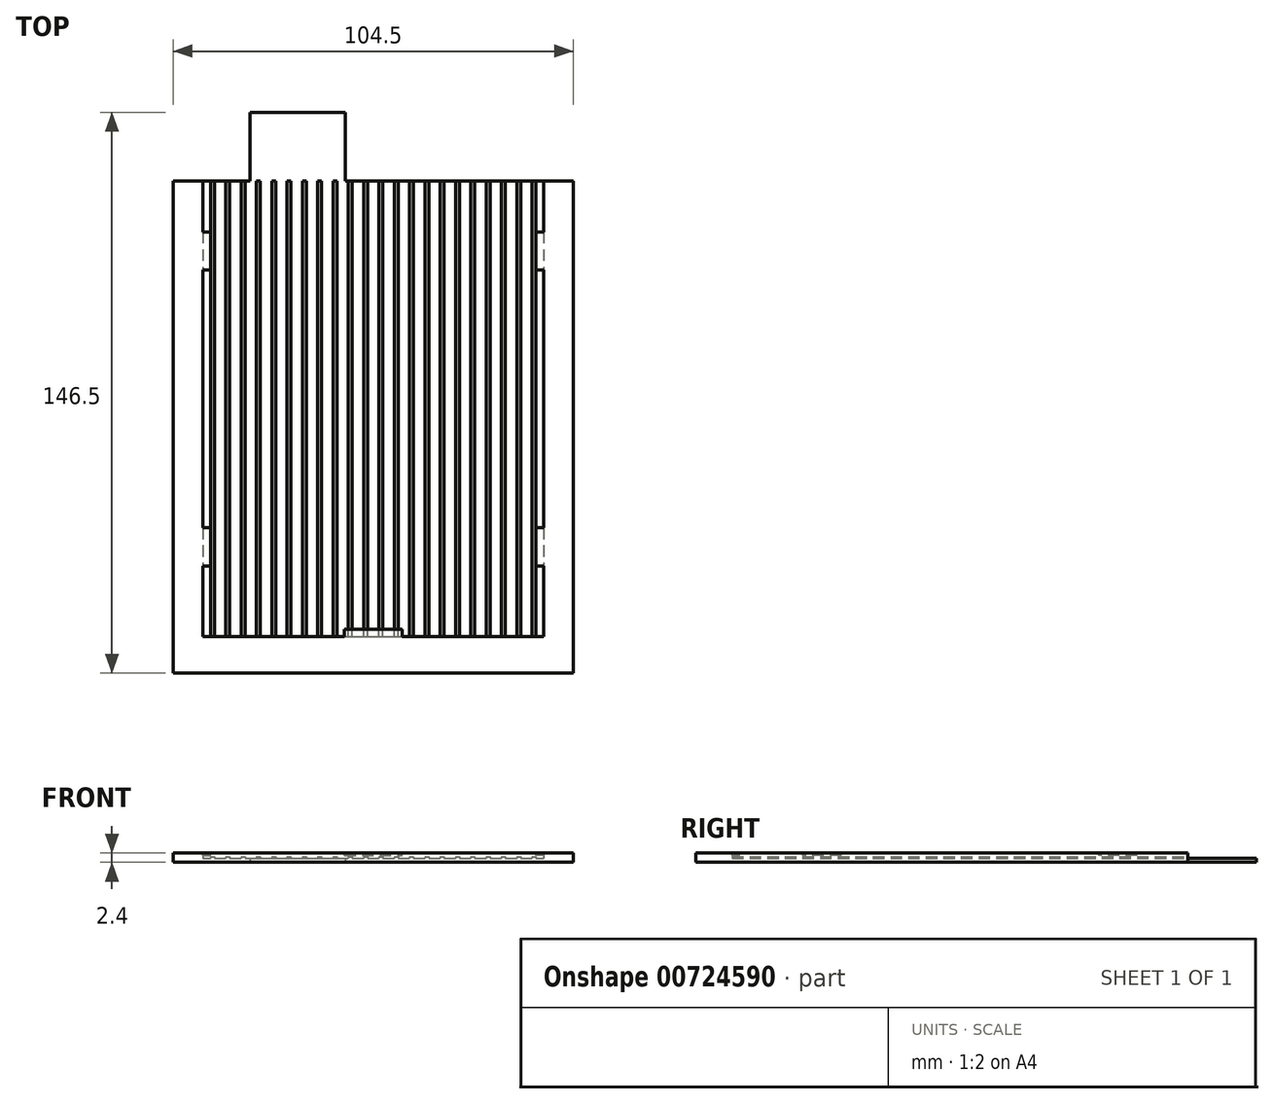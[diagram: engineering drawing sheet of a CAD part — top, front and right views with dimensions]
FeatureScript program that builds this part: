
annotation { "Feature Type Name" : "Feature", "Feature Type Description" : "" }
export const myFeature = defineFeature(function(context is Context, id is Id, definition is map)
    precondition{}
    {
        {
            var Q0;
            Q0=qCreatedBy(makeId("Top.planeOp"),FACE);
            var sketch = newSketch(context, id + "F0", { "sketchPlane" : qUnion([Q0])});
            skLineSegment(sketch, "E0.bottom", {"start": v(-45, 88.97) * mm, "end": v(-25, 88.97) * mm});
            skLineSegment(sketch, "E0.top", {"start": v(-45, -39.53) * mm, "end": v(59.5, -39.53) * mm});
            skLineSegment(sketch, "E0.left", {"start": v(-45, 88.97) * mm, "end": v(-45, -39.53) * mm});
            skLineSegment(sketch, "E0.right", {"start": v(59.5, 88.97) * mm, "end": v(59.5, -39.53) * mm});
            skLineSegment(sketch, "E1.top", {"start": v(-25, 106.97) * mm, "end": v(0, 106.97) * mm});
            skLineSegment(sketch, "E1.left", {"start": v(-25, 88.97) * mm, "end": v(-25, 106.97) * mm});
            skLineSegment(sketch, "E1.right", {"start": v(0, 88.97) * mm, "end": v(0, 106.97) * mm});
            skLineSegment(sketch, "E2.trimOffspring", {"start": v(0, 88.97) * mm, "end": v(59.5, 88.97) * mm});
            skSolve(sketch);
        }
        {
            var Q0;
            Q0=makeQuery(id+"F0.imprint","IMPRINT",FACE,{"disambiguationData":[TD([[makeQuery(id+"F0.imprint","IMPRINT",EDGE,{"derivedFrom":sQuery(id+"F0.wireOp",EDGE,"E0.bottom")}),-1.0]])]});
            extrude(context, id + "F1", {"entities" : qUnion([Q0]), "depth" : 1 * mm, "offsetDistance" : 25 * mm});
        }
        {
            var Q0;
            Q0=makeQuery(id+"F1.opExtrude","CAP_FACE",FACE,{"disambiguationData":[OSD([sQuery(id+"F0.wireOp",EDGE,"E0.bottom"),sQuery(id+"F0.wireOp",EDGE,"E0.top"),sQuery(id+"F0.wireOp",EDGE,"E0.left"),sQuery(id+"F0.wireOp",EDGE,"E0.right")])],"isStart":false});
            var sketch = newSketch(context, id + "F2", { "sketchPlane" : qUnion([Q0])});
            skLineSegment(sketch, "E3.bottom", {"start": v(-37.25, 88.97) * mm, "end": v(51.75, 88.97) * mm});
            skLineSegment(sketch, "E3.top", {"start": v(-37.25, -30.03) * mm, "end": v(51.75, -30.03) * mm});
            skLineSegment(sketch, "E3.left", {"start": v(-37.25, 88.97) * mm, "end": v(-37.25, -30.03) * mm});
            skLineSegment(sketch, "E3.right", {"start": v(51.75, 88.97) * mm, "end": v(51.75, -30.03) * mm});
            skSolve(sketch);
        }
        {
            var Q0;
            Q0=makeQuery(id+"F2.imprint","IMPRINT",FACE,{"disambiguationData":[TD([[makeQuery(id+"F2.imprint","IMPRINT",EDGE,{"derivedFrom":sQuery(id+"F2.wireOp",EDGE,"E3.top")}),-1.0]])]});
            extrude(context, id + "F3", {"entities" : qUnion([Q0]), "operationType" : NewBodyOperationType.ADD, "depth" : 1.4 * mm, "offsetDistance" : 25 * mm});
        }
        {
            var Q0;
            Q0=makeQuery(id+"F3.opExtrude","CAP_FACE",FACE,{"disambiguationData":[OSD([sQuery(id+"F0.wireOp",EDGE,"E0.bottom"),sQuery(id+"F0.wireOp",EDGE,"E0.top"),sQuery(id+"F0.wireOp",EDGE,"E0.left"),sQuery(id+"F0.wireOp",EDGE,"E0.right"),sQuery(id+"F0.wireOp",EDGE,"E2.trimOffspring"),sQuery(id+"F2.wireOp",EDGE,"E3.top"),sQuery(id+"F2.wireOp",EDGE,"E3.left"),sQuery(id+"F2.wireOp",EDGE,"E3.right")])],"isStart":false});
            var sketch = newSketch(context, id + "F4", { "sketchPlane" : qUnion([Q0])});
            skLineSegment(sketch, "E4.bottom", {"start": v(-37.25, 75.74) * mm, "end": v(-35.25, 75.74) * mm});
            skLineSegment(sketch, "E4.top", {"start": v(-37.25, 65.74) * mm, "end": v(-35.25, 65.74) * mm});
            skLineSegment(sketch, "E4.left", {"start": v(-37.25, 75.74) * mm, "end": v(-37.25, 65.74) * mm});
            skLineSegment(sketch, "E4.right", {"start": v(-35.25, 75.74) * mm, "end": v(-35.25, 65.74) * mm});
            skLineSegment(sketch, "E5.bottom", {"start": v(51.75, 75.74) * mm, "end": v(49.75, 75.74) * mm});
            skLineSegment(sketch, "E5.top", {"start": v(51.75, 65.74) * mm, "end": v(49.75, 65.74) * mm});
            skLineSegment(sketch, "E5.left", {"start": v(51.75, 75.74) * mm, "end": v(51.75, 65.74) * mm});
            skLineSegment(sketch, "E5.right", {"start": v(49.75, 75.74) * mm, "end": v(49.75, 65.74) * mm});
            skLineSegment(sketch, "E6.bottom", {"start": v(-37.25, -1.52) * mm, "end": v(-35.25, -1.52) * mm});
            skLineSegment(sketch, "E6.top", {"start": v(-37.25, -11.52) * mm, "end": v(-35.25, -11.52) * mm});
            skLineSegment(sketch, "E6.left", {"start": v(-37.25, -1.52) * mm, "end": v(-37.25, -11.52) * mm});
            skLineSegment(sketch, "E6.right", {"start": v(-35.25, -1.52) * mm, "end": v(-35.25, -11.52) * mm});
            skLineSegment(sketch, "E7.bottom", {"start": v(49.75, -1.52) * mm, "end": v(51.75, -1.52) * mm});
            skLineSegment(sketch, "E7.top", {"start": v(49.75, -11.52) * mm, "end": v(51.75, -11.52) * mm});
            skLineSegment(sketch, "E7.left", {"start": v(49.75, -1.52) * mm, "end": v(49.75, -11.52) * mm});
            skLineSegment(sketch, "E7.right", {"start": v(51.75, -1.52) * mm, "end": v(51.75, -11.52) * mm});
            skLineSegment(sketch, "E8.bottom", {"start": v(-0.25, -30.03) * mm, "end": v(14.75, -30.03) * mm});
            skLineSegment(sketch, "E8.top", {"start": v(-0.25, -28.03) * mm, "end": v(14.75, -28.03) * mm});
            skLineSegment(sketch, "E8.left", {"start": v(-0.25, -30.03) * mm, "end": v(-0.25, -28.03) * mm});
            skLineSegment(sketch, "E8.right", {"start": v(14.75, -30.03) * mm, "end": v(14.75, -28.03) * mm});
            skSolve(sketch);
        }
        {
            var Q0;
            Q0=makeQuery(id+"F4.imprint","IMPRINT",FACE,{"disambiguationData":[TD([[makeQuery(id+"F4.imprint","IMPRINT",EDGE,{"derivedFrom":sQuery(id+"F4.wireOp",EDGE,"E5.bottom")}),1.0]])]});
            var Q1;
            Q1=makeQuery(id+"F4.imprint","IMPRINT",FACE,{"disambiguationData":[TD([[makeQuery(id+"F4.imprint","IMPRINT",EDGE,{"derivedFrom":sQuery(id+"F4.wireOp",EDGE,"E7.bottom")}),-1.0]])]});
            var Q2;
            Q2=makeQuery(id+"F4.imprint","IMPRINT",FACE,{"disambiguationData":[TD([[makeQuery(id+"F4.imprint","IMPRINT",EDGE,{"derivedFrom":sQuery(id+"F4.wireOp",EDGE,"E8.bottom")}),1.0]])]});
            var Q3;
            Q3=makeQuery(id+"F4.imprint","IMPRINT",FACE,{"disambiguationData":[TD([[makeQuery(id+"F4.imprint","IMPRINT",EDGE,{"derivedFrom":sQuery(id+"F4.wireOp",EDGE,"E6.bottom")}),-1.0]])]});
            var Q4;
            Q4=makeQuery(id+"F4.imprint","IMPRINT",FACE,{"disambiguationData":[TD([[makeQuery(id+"F4.imprint","IMPRINT",EDGE,{"derivedFrom":sQuery(id+"F4.wireOp",EDGE,"E4.bottom")}),-1.0]])]});
            extrude(context, id + "F5", {"entities" : qUnion([Q0, Q1, Q2, Q3, Q4]), "operationType" : NewBodyOperationType.ADD, "depth" : -.6 * mm, "offsetDistance" : 25 * mm});
        }
        {
            var Q0;
            Q0=makeQuery(id+"F1.opExtrude","CAP_FACE",FACE,{"disambiguationData":[OSD([sQuery(id+"F0.wireOp",EDGE,"E0.bottom"),sQuery(id+"F0.wireOp",EDGE,"E0.top"),sQuery(id+"F0.wireOp",EDGE,"E0.left"),sQuery(id+"F0.wireOp",EDGE,"E0.right"),sQuery(id+"F0.wireOp",EDGE,"E1.top"),sQuery(id+"F0.wireOp",EDGE,"E1.left"),sQuery(id+"F0.wireOp",EDGE,"E1.right"),sQuery(id+"F0.wireOp",EDGE,"E2.trimOffspring")])],"isStart":false});
            var sketch = newSketch(context, id + "F6", { "sketchPlane" : qUnion([Q0])});
            skLineSegment(sketch, "E9.bottom", {"start": v(-35.25, -30.03) * mm, "end": v(-34.25, -30.03) * mm});
            skLineSegment(sketch, "E9.top", {"start": v(-35.25, 88.97) * mm, "end": v(-34.25, 88.97) * mm});
            skLineSegment(sketch, "E9.left", {"start": v(-35.25, -30.03) * mm, "end": v(-35.25, 88.97) * mm});
            skLineSegment(sketch, "E9.right", {"start": v(-34.25, -30.03) * mm, "end": v(-34.25, 88.97) * mm});
            skLineSegment(sketch, "E10.1.0.0", {"start": v(-30.25, -30.03) * mm, "end": v(-30.25, 88.97) * mm});
            skLineSegment(sketch, "E10.1.0.1", {"start": v(-31.25, -30.03) * mm, "end": v(-31.25, 88.97) * mm});
            skLineSegment(sketch, "E10.1.0.2", {"start": v(-31.25, 88.97) * mm, "end": v(-30.25, 88.97) * mm});
            skLineSegment(sketch, "E10.1.0.3", {"start": v(-31.25, -30.03) * mm, "end": v(-30.25, -30.03) * mm});
            skLineSegment(sketch, "E10.2.0.0", {"start": v(-26.25, -30.03) * mm, "end": v(-26.25, 88.97) * mm});
            skLineSegment(sketch, "E10.2.0.1", {"start": v(-27.25, -30.03) * mm, "end": v(-27.25, 88.97) * mm});
            skLineSegment(sketch, "E10.2.0.2", {"start": v(-27.25, 88.97) * mm, "end": v(-26.25, 88.97) * mm});
            skLineSegment(sketch, "E10.2.0.3", {"start": v(-27.25, -30.03) * mm, "end": v(-26.25, -30.03) * mm});
            skLineSegment(sketch, "E10.3.0.0", {"start": v(-22.25, -30.03) * mm, "end": v(-22.25, 88.97) * mm});
            skLineSegment(sketch, "E10.3.0.1", {"start": v(-23.25, -30.03) * mm, "end": v(-23.25, 88.97) * mm});
            skLineSegment(sketch, "E10.3.0.2", {"start": v(-23.25, 88.97) * mm, "end": v(-22.25, 88.97) * mm});
            skLineSegment(sketch, "E10.3.0.3", {"start": v(-23.25, -30.03) * mm, "end": v(-22.25, -30.03) * mm});
            skLineSegment(sketch, "E10.4.0.0", {"start": v(-18.25, -30.03) * mm, "end": v(-18.25, 88.97) * mm});
            skLineSegment(sketch, "E10.4.0.1", {"start": v(-19.25, -30.03) * mm, "end": v(-19.25, 88.97) * mm});
            skLineSegment(sketch, "E10.4.0.2", {"start": v(-19.25, 88.97) * mm, "end": v(-18.25, 88.97) * mm});
            skLineSegment(sketch, "E10.4.0.3", {"start": v(-19.25, -30.03) * mm, "end": v(-18.25, -30.03) * mm});
            skLineSegment(sketch, "E10.5.0.0", {"start": v(-14.25, -30.03) * mm, "end": v(-14.25, 88.97) * mm});
            skLineSegment(sketch, "E10.5.0.1", {"start": v(-15.25, -30.03) * mm, "end": v(-15.25, 88.97) * mm});
            skLineSegment(sketch, "E10.5.0.2", {"start": v(-15.25, 88.97) * mm, "end": v(-14.25, 88.97) * mm});
            skLineSegment(sketch, "E10.5.0.3", {"start": v(-15.25, -30.03) * mm, "end": v(-14.25, -30.03) * mm});
            skLineSegment(sketch, "E10.6.0.0", {"start": v(-10.25, -30.03) * mm, "end": v(-10.25, 88.97) * mm});
            skLineSegment(sketch, "E10.6.0.1", {"start": v(-11.25, -30.03) * mm, "end": v(-11.25, 88.97) * mm});
            skLineSegment(sketch, "E10.6.0.2", {"start": v(-11.25, 88.97) * mm, "end": v(-10.25, 88.97) * mm});
            skLineSegment(sketch, "E10.6.0.3", {"start": v(-11.25, -30.03) * mm, "end": v(-10.25, -30.03) * mm});
            skLineSegment(sketch, "E10.7.0.0", {"start": v(-6.25, -30.03) * mm, "end": v(-6.25, 88.97) * mm});
            skLineSegment(sketch, "E10.7.0.1", {"start": v(-7.25, -30.03) * mm, "end": v(-7.25, 88.97) * mm});
            skLineSegment(sketch, "E10.7.0.2", {"start": v(-7.25, 88.97) * mm, "end": v(-6.25, 88.97) * mm});
            skLineSegment(sketch, "E10.7.0.3", {"start": v(-7.25, -30.03) * mm, "end": v(-6.25, -30.03) * mm});
            skLineSegment(sketch, "E10.8.0.0", {"start": v(-2.25, -30.03) * mm, "end": v(-2.25, 88.97) * mm});
            skLineSegment(sketch, "E10.8.0.1", {"start": v(-3.25, -30.03) * mm, "end": v(-3.25, 88.97) * mm});
            skLineSegment(sketch, "E10.8.0.2", {"start": v(-3.25, 88.97) * mm, "end": v(-2.25, 88.97) * mm});
            skLineSegment(sketch, "E10.8.0.3", {"start": v(-3.25, -30.03) * mm, "end": v(-2.25, -30.03) * mm});
            skLineSegment(sketch, "E10.9.0.0", {"start": v(1.75, -30.03) * mm, "end": v(1.75, 88.97) * mm});
            skLineSegment(sketch, "E10.9.0.1", {"start": v(0.75, -30.03) * mm, "end": v(0.75, 88.97) * mm});
            skLineSegment(sketch, "E10.9.0.2", {"start": v(0.75, 88.97) * mm, "end": v(1.75, 88.97) * mm});
            skLineSegment(sketch, "E10.9.0.3", {"start": v(0.75, -30.03) * mm, "end": v(1.75, -30.03) * mm});
            skLineSegment(sketch, "E10.direction1", {"start": v(-35.25, -30.03) * mm, "end": v(-31.25, -30.03) * mm, "construction": true});
            skLineSegment(sketch, "E11.0.10.0", {"start": v(5.75, -30.03) * mm, "end": v(5.75, 88.97) * mm});
            skLineSegment(sketch, "E11.3.10.0", {"start": v(4.75, -30.03) * mm, "end": v(4.75, 88.97) * mm});
            skLineSegment(sketch, "E11.6.10.0", {"start": v(4.75, 88.97) * mm, "end": v(5.75, 88.97) * mm});
            skLineSegment(sketch, "E11.9.10.0", {"start": v(4.75, -30.03) * mm, "end": v(5.75, -30.03) * mm});
            skLineSegment(sketch, "E11.0.11.0", {"start": v(9.75, -30.03) * mm, "end": v(9.75, 88.97) * mm});
            skLineSegment(sketch, "E11.3.11.0", {"start": v(8.75, -30.03) * mm, "end": v(8.75, 88.97) * mm});
            skLineSegment(sketch, "E11.6.11.0", {"start": v(8.75, 88.97) * mm, "end": v(9.75, 88.97) * mm});
            skLineSegment(sketch, "E11.9.11.0", {"start": v(8.75, -30.03) * mm, "end": v(9.75, -30.03) * mm});
            skLineSegment(sketch, "E11.0.12.0", {"start": v(13.75, -30.03) * mm, "end": v(13.75, 88.97) * mm});
            skLineSegment(sketch, "E11.3.12.0", {"start": v(12.75, -30.03) * mm, "end": v(12.75, 88.97) * mm});
            skLineSegment(sketch, "E11.6.12.0", {"start": v(12.75, 88.97) * mm, "end": v(13.75, 88.97) * mm});
            skLineSegment(sketch, "E11.9.12.0", {"start": v(12.75, -30.03) * mm, "end": v(13.75, -30.03) * mm});
            skLineSegment(sketch, "E11.0.13.0", {"start": v(17.75, -30.03) * mm, "end": v(17.75, 88.97) * mm});
            skLineSegment(sketch, "E11.3.13.0", {"start": v(16.75, -30.03) * mm, "end": v(16.75, 88.97) * mm});
            skLineSegment(sketch, "E11.6.13.0", {"start": v(16.75, 88.97) * mm, "end": v(17.75, 88.97) * mm});
            skLineSegment(sketch, "E11.9.13.0", {"start": v(16.75, -30.03) * mm, "end": v(17.75, -30.03) * mm});
            skLineSegment(sketch, "E12.0.14.0", {"start": v(21.75, -30.03) * mm, "end": v(21.75, 88.97) * mm});
            skLineSegment(sketch, "E12.3.14.0", {"start": v(20.75, -30.03) * mm, "end": v(20.75, 88.97) * mm});
            skLineSegment(sketch, "E12.6.14.0", {"start": v(20.75, 88.97) * mm, "end": v(21.75, 88.97) * mm});
            skLineSegment(sketch, "E12.9.14.0", {"start": v(20.75, -30.03) * mm, "end": v(21.75, -30.03) * mm});
            skLineSegment(sketch, "E12.0.15.0", {"start": v(25.75, -30.03) * mm, "end": v(25.75, 88.97) * mm});
            skLineSegment(sketch, "E12.3.15.0", {"start": v(24.75, -30.03) * mm, "end": v(24.75, 88.97) * mm});
            skLineSegment(sketch, "E12.6.15.0", {"start": v(24.75, 88.97) * mm, "end": v(25.75, 88.97) * mm});
            skLineSegment(sketch, "E12.9.15.0", {"start": v(24.75, -30.03) * mm, "end": v(25.75, -30.03) * mm});
            skLineSegment(sketch, "E12.0.16.0", {"start": v(29.75, -30.03) * mm, "end": v(29.75, 88.97) * mm});
            skLineSegment(sketch, "E12.3.16.0", {"start": v(28.75, -30.03) * mm, "end": v(28.75, 88.97) * mm});
            skLineSegment(sketch, "E12.6.16.0", {"start": v(28.75, 88.97) * mm, "end": v(29.75, 88.97) * mm});
            skLineSegment(sketch, "E12.9.16.0", {"start": v(28.75, -30.03) * mm, "end": v(29.75, -30.03) * mm});
            skLineSegment(sketch, "E12.0.17.0", {"start": v(33.75, -30.03) * mm, "end": v(33.75, 88.97) * mm});
            skLineSegment(sketch, "E12.3.17.0", {"start": v(32.75, -30.03) * mm, "end": v(32.75, 88.97) * mm});
            skLineSegment(sketch, "E12.6.17.0", {"start": v(32.75, 88.97) * mm, "end": v(33.75, 88.97) * mm});
            skLineSegment(sketch, "E12.9.17.0", {"start": v(32.75, -30.03) * mm, "end": v(33.75, -30.03) * mm});
            skLineSegment(sketch, "E12.0.18.0", {"start": v(37.75, -30.03) * mm, "end": v(37.75, 88.97) * mm});
            skLineSegment(sketch, "E12.3.18.0", {"start": v(36.75, -30.03) * mm, "end": v(36.75, 88.97) * mm});
            skLineSegment(sketch, "E12.6.18.0", {"start": v(36.75, 88.97) * mm, "end": v(37.75, 88.97) * mm});
            skLineSegment(sketch, "E12.9.18.0", {"start": v(36.75, -30.03) * mm, "end": v(37.75, -30.03) * mm});
            skLineSegment(sketch, "E12.0.19.0", {"start": v(41.75, -30.03) * mm, "end": v(41.75, 88.97) * mm});
            skLineSegment(sketch, "E12.3.19.0", {"start": v(40.75, -30.03) * mm, "end": v(40.75, 88.97) * mm});
            skLineSegment(sketch, "E12.6.19.0", {"start": v(40.75, 88.97) * mm, "end": v(41.75, 88.97) * mm});
            skLineSegment(sketch, "E12.9.19.0", {"start": v(40.75, -30.03) * mm, "end": v(41.75, -30.03) * mm});
            skLineSegment(sketch, "E13.0.20.0", {"start": v(45.75, -30.03) * mm, "end": v(45.75, 88.97) * mm});
            skLineSegment(sketch, "E13.3.20.0", {"start": v(44.75, -30.03) * mm, "end": v(44.75, 88.97) * mm});
            skLineSegment(sketch, "E13.6.20.0", {"start": v(44.75, 88.97) * mm, "end": v(45.75, 88.97) * mm});
            skLineSegment(sketch, "E13.9.20.0", {"start": v(44.75, -30.03) * mm, "end": v(45.75, -30.03) * mm});
            skLineSegment(sketch, "E13.0.21.0", {"start": v(49.75, -30.03) * mm, "end": v(49.75, 88.97) * mm});
            skLineSegment(sketch, "E13.3.21.0", {"start": v(48.75, -30.03) * mm, "end": v(48.75, 88.97) * mm});
            skLineSegment(sketch, "E13.6.21.0", {"start": v(48.75, 88.97) * mm, "end": v(49.75, 88.97) * mm});
            skLineSegment(sketch, "E13.9.21.0", {"start": v(48.75, -30.03) * mm, "end": v(49.75, -30.03) * mm});
            skSolve(sketch);
        }
        {
            var Q0;
            Q0=makeQuery(id+"F6.imprint","IMPRINT",FACE,{"disambiguationData":[TD([[makeQuery(id+"F6.imprint","IMPRINT",EDGE,{"derivedFrom":sQuery(id+"F6.wireOp",EDGE,"E9.bottom")}),1.0]])]});
            var Q1;
            Q1=makeQuery(id+"F6.imprint","IMPRINT",FACE,{"disambiguationData":[TD([[makeQuery(id+"F6.imprint","IMPRINT",EDGE,{"derivedFrom":sQuery(id+"F6.wireOp",EDGE,"E10.1.0.0")}),1.0]])]});
            var Q2;
            Q2=makeQuery(id+"F6.imprint","IMPRINT",FACE,{"disambiguationData":[TD([[makeQuery(id+"F6.imprint","IMPRINT",EDGE,{"derivedFrom":sQuery(id+"F6.wireOp",EDGE,"E10.2.0.0")}),1.0]])]});
            var Q3;
            Q3=makeQuery(id+"F6.imprint","IMPRINT",FACE,{"disambiguationData":[TD([[makeQuery(id+"F6.imprint","IMPRINT",EDGE,{"derivedFrom":sQuery(id+"F6.wireOp",EDGE,"E10.3.0.0")}),1.0]])]});
            var Q4;
            Q4=makeQuery(id+"F6.imprint","IMPRINT",FACE,{"disambiguationData":[TD([[makeQuery(id+"F6.imprint","IMPRINT",EDGE,{"derivedFrom":sQuery(id+"F6.wireOp",EDGE,"E10.4.0.0")}),1.0]])]});
            var Q5;
            Q5=makeQuery(id+"F6.imprint","IMPRINT",FACE,{"disambiguationData":[TD([[makeQuery(id+"F6.imprint","IMPRINT",EDGE,{"derivedFrom":sQuery(id+"F6.wireOp",EDGE,"E10.5.0.0")}),1.0]])]});
            var Q6;
            Q6=makeQuery(id+"F6.imprint","IMPRINT",FACE,{"disambiguationData":[TD([[makeQuery(id+"F6.imprint","IMPRINT",EDGE,{"derivedFrom":sQuery(id+"F6.wireOp",EDGE,"E10.6.0.0")}),1.0]])]});
            var Q7;
            Q7=makeQuery(id+"F6.imprint","IMPRINT",FACE,{"disambiguationData":[TD([[makeQuery(id+"F6.imprint","IMPRINT",EDGE,{"derivedFrom":sQuery(id+"F6.wireOp",EDGE,"E10.7.0.0")}),1.0]])]});
            var Q8;
            Q8=makeQuery(id+"F6.imprint","IMPRINT",FACE,{"disambiguationData":[TD([[makeQuery(id+"F6.imprint","IMPRINT",EDGE,{"derivedFrom":sQuery(id+"F6.wireOp",EDGE,"E10.8.0.0")}),1.0]])]});
            var Q9;
            Q9=makeQuery(id+"F6.imprint","IMPRINT",FACE,{"disambiguationData":[TD([[makeQuery(id+"F6.imprint","IMPRINT",EDGE,{"derivedFrom":sQuery(id+"F6.wireOp",EDGE,"E10.9.0.0")}),1.0]])]});
            var Q10;
            Q10=makeQuery(id+"F6.imprint","IMPRINT",FACE,{"disambiguationData":[TD([[makeQuery(id+"F6.imprint","IMPRINT",EDGE,{"derivedFrom":sQuery(id+"F6.wireOp",EDGE,"E11.0.10.0")}),1.0]])]});
            var Q11;
            Q11=makeQuery(id+"F6.imprint","IMPRINT",FACE,{"disambiguationData":[TD([[makeQuery(id+"F6.imprint","IMPRINT",EDGE,{"derivedFrom":sQuery(id+"F6.wireOp",EDGE,"E11.0.11.0")}),1.0]])]});
            var Q12;
            Q12=makeQuery(id+"F6.imprint","IMPRINT",FACE,{"disambiguationData":[TD([[makeQuery(id+"F6.imprint","IMPRINT",EDGE,{"derivedFrom":sQuery(id+"F6.wireOp",EDGE,"E11.0.12.0")}),1.0]])]});
            var Q13;
            Q13=makeQuery(id+"F6.imprint","IMPRINT",FACE,{"disambiguationData":[TD([[makeQuery(id+"F6.imprint","IMPRINT",EDGE,{"derivedFrom":sQuery(id+"F6.wireOp",EDGE,"E11.0.13.0")}),1.0]])]});
            var Q14;
            Q14=makeQuery(id+"F6.imprint","IMPRINT",FACE,{"disambiguationData":[TD([[makeQuery(id+"F6.imprint","IMPRINT",EDGE,{"derivedFrom":sQuery(id+"F6.wireOp",EDGE,"E12.0.14.0")}),1.0]])]});
            var Q15;
            Q15=makeQuery(id+"F6.imprint","IMPRINT",FACE,{"disambiguationData":[TD([[makeQuery(id+"F6.imprint","IMPRINT",EDGE,{"derivedFrom":sQuery(id+"F6.wireOp",EDGE,"E12.0.15.0")}),1.0]])]});
            var Q16;
            Q16=makeQuery(id+"F6.imprint","IMPRINT",FACE,{"disambiguationData":[TD([[makeQuery(id+"F6.imprint","IMPRINT",EDGE,{"derivedFrom":sQuery(id+"F6.wireOp",EDGE,"E12.0.16.0")}),1.0]])]});
            var Q17;
            Q17=makeQuery(id+"F6.imprint","IMPRINT",FACE,{"disambiguationData":[TD([[makeQuery(id+"F6.imprint","IMPRINT",EDGE,{"derivedFrom":sQuery(id+"F6.wireOp",EDGE,"E12.0.17.0")}),1.0]])]});
            var Q18;
            Q18=makeQuery(id+"F6.imprint","IMPRINT",FACE,{"disambiguationData":[TD([[makeQuery(id+"F6.imprint","IMPRINT",EDGE,{"derivedFrom":sQuery(id+"F6.wireOp",EDGE,"E12.0.18.0")}),1.0]])]});
            var Q19;
            Q19=makeQuery(id+"F6.imprint","IMPRINT",FACE,{"disambiguationData":[TD([[makeQuery(id+"F6.imprint","IMPRINT",EDGE,{"derivedFrom":sQuery(id+"F6.wireOp",EDGE,"E12.0.19.0")}),1.0]])]});
            var Q20;
            Q20=makeQuery(id+"F6.imprint","IMPRINT",FACE,{"disambiguationData":[TD([[makeQuery(id+"F6.imprint","IMPRINT",EDGE,{"derivedFrom":sQuery(id+"F6.wireOp",EDGE,"E13.0.21.0")}),1.0]])]});
            var Q21;
            Q21=makeQuery(id+"F6.imprint","IMPRINT",FACE,{"disambiguationData":[TD([[makeQuery(id+"F6.imprint","IMPRINT",EDGE,{"derivedFrom":sQuery(id+"F6.wireOp",EDGE,"E13.0.20.0")}),1.0]])]});
            extrude(context, id + "F7", {"entities" : qUnion([Q0, Q1, Q2, Q3, Q4, Q5, Q6, Q7, Q8, Q9, Q10, Q11, Q12, Q13, Q14, Q15, Q16, Q17, Q18, Q19, Q20, Q21]), "operationType" : NewBodyOperationType.ADD, "depth" : .4 * mm, "offsetDistance" : 25 * mm});
        }
    });
